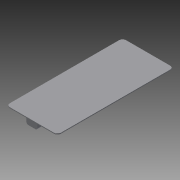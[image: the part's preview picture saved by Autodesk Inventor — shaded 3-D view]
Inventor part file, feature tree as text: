
AUTODESK INVENTOR PART (.ipt)
format: ipt  version: 2014 (Build 180170000, 170)  size: 112,640 bytes
history: native  units: in
note: dims shown in document units (in); Inventor stores cm internally (conversion verified against a paired STEP export)
features: fillet x2, plane x1, extrude x1, sketch x1, reference x1
ambient origin geometry x8: Origin, YZ Plane, XZ Plane, XY Plane, X Axis, Y Axis, Z Axis, Center Point
bodies: Solid1 (feature_tree)
feature tree (6):
  plane  "Work Plane1"
  extrude  "Extrusion1"  Depth=0.1in
  fillet  "Fillet1"  Radius=0.001in
  fillet  "Fillet2"  Radius=0.0236in
  sketch  "Sketch1"  dims[d0=0.025in d1=0.025in d2=0.001in d3=0.0236in d4=0.02in d5=0.02in d6=0.001in d7=3.3in d8=0.0in d9=0.05in d10=0.1in]
  reference  "Reference1"
